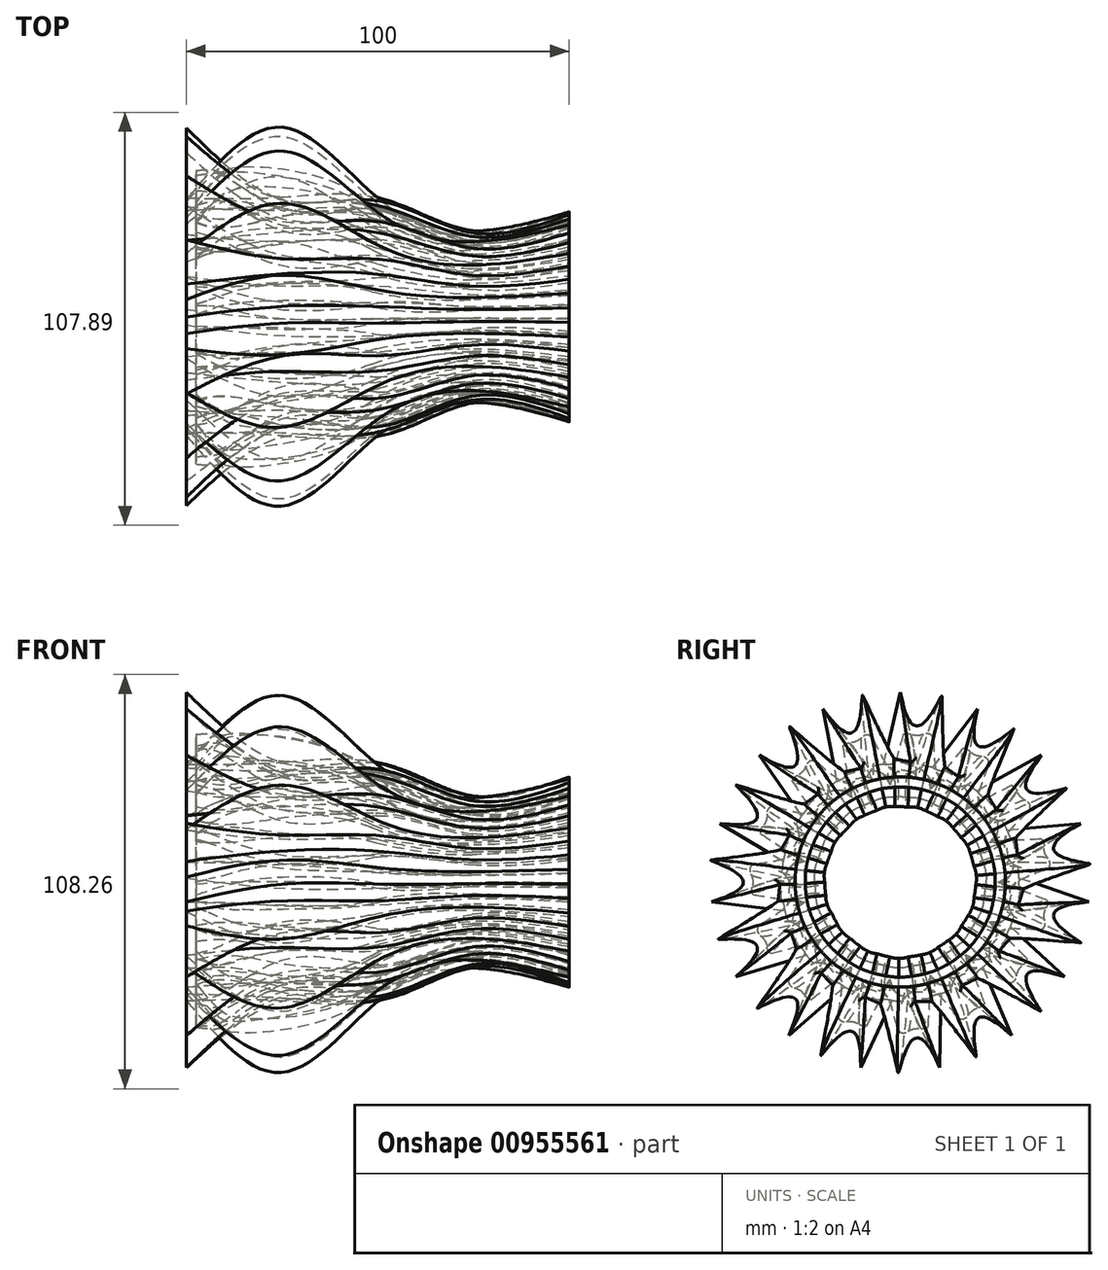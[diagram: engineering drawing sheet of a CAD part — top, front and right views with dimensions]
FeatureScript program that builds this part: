
annotation { "Feature Type Name" : "Feature", "Feature Type Description" : "" }
export const myFeature = defineFeature(function(context is Context, id is Id, definition is map)
    precondition{}
    {
        {
            var Q0;
            Q0=qCreatedBy(makeId("Right.planeOp"),FACE);
            var sketch = newSketch(context, id + "F0", { "sketchPlane" : qUnion([Q0])});
            skCircle(sketch, "E0", {"center": v(0, 0) * mm, "radius": 31.06 * mm});
            skLineSegment(sketch, "E1", {"start": v(-4.34, 30.75) * mm, "end": v(0, 49.56) * mm});
            skLineSegment(sketch, "E2", {"start": v(0, 49.56) * mm, "end": v(4.53, 30.72) * mm});
            skLineSegment(sketch, "E3.1.0", {"start": v(-20.16, 45.27) * mm, "end": v(-8.36, 29.91) * mm});
            skLineSegment(sketch, "E3.1.1", {"start": v(-16.47, 26.33) * mm, "end": v(-20.16, 45.27) * mm});
            skLineSegment(sketch, "E3.2.0", {"start": v(-36.83, 33.16) * mm, "end": v(-19.8, 23.92) * mm});
            skLineSegment(sketch, "E3.2.1", {"start": v(-25.76, 17.35) * mm, "end": v(-36.83, 33.16) * mm});
            skLineSegment(sketch, "E3.3.0", {"start": v(-47.13, 15.31) * mm, "end": v(-27.82, 13.8) * mm});
            skLineSegment(sketch, "E3.3.1", {"start": v(-30.59, 5.38) * mm, "end": v(-47.13, 15.31) * mm});
            skLineSegment(sketch, "E3.4.0", {"start": v(-49.29, -5.18) * mm, "end": v(-31.03, 1.3) * mm});
            skLineSegment(sketch, "E3.4.1", {"start": v(-30.13, -7.53) * mm, "end": v(-49.29, -5.18) * mm});
            skLineSegment(sketch, "E3.5.0", {"start": v(-42.92, -24.78) * mm, "end": v(-28.87, -11.44) * mm});
            skLineSegment(sketch, "E3.5.1", {"start": v(-24.46, -19.13) * mm, "end": v(-42.92, -24.78) * mm});
            skLineSegment(sketch, "E3.6.0", {"start": v(-29.13, -40.1) * mm, "end": v(-21.72, -22.2) * mm});
            skLineSegment(sketch, "E3.6.1", {"start": v(-14.56, -27.43) * mm, "end": v(-29.13, -40.1) * mm});
            skLineSegment(sketch, "E3.7.0", {"start": v(-10.3, -48.48) * mm, "end": v(-10.82, -29.11) * mm});
            skLineSegment(sketch, "E3.7.1", {"start": v(-2.15, -30.98) * mm, "end": v(-10.3, -48.48) * mm});
            skLineSegment(sketch, "E3.8.0", {"start": v(10.3, -48.48) * mm, "end": v(1.96, -31) * mm});
            skLineSegment(sketch, "E3.8.1", {"start": v(10.64, -29.18) * mm, "end": v(10.3, -48.48) * mm});
            skLineSegment(sketch, "E3.9.0", {"start": v(29.13, -40.1) * mm, "end": v(14.4, -27.52) * mm});
            skLineSegment(sketch, "E3.9.1", {"start": v(21.59, -22.33) * mm, "end": v(29.13, -40.1) * mm});
            skLineSegment(sketch, "E3.10.0", {"start": v(42.92, -24.78) * mm, "end": v(24.34, -19.29) * mm});
            skLineSegment(sketch, "E3.10.1", {"start": v(28.8, -11.62) * mm, "end": v(42.92, -24.78) * mm});
            skLineSegment(sketch, "E3.11.0", {"start": v(49.29, -5.18) * mm, "end": v(30.08, -7.72) * mm});
            skLineSegment(sketch, "E3.11.1", {"start": v(31.04, 1.1) * mm, "end": v(49.29, -5.18) * mm});
            skLineSegment(sketch, "E3.12.0", {"start": v(47.13, 15.31) * mm, "end": v(30.62, 5.19) * mm});
            skLineSegment(sketch, "E3.12.1", {"start": v(27.9, 13.63) * mm, "end": v(47.13, 15.31) * mm});
            skLineSegment(sketch, "E3.13.0", {"start": v(36.83, 33.16) * mm, "end": v(25.86, 17.2) * mm});
            skLineSegment(sketch, "E3.13.1", {"start": v(19.95, 23.8) * mm, "end": v(36.83, 33.16) * mm});
            skLineSegment(sketch, "E3.14.0", {"start": v(20.16, 45.27) * mm, "end": v(16.64, 26.22) * mm});
            skLineSegment(sketch, "E3.14.1", {"start": v(8.54, 29.86) * mm, "end": v(20.16, 45.27) * mm});
            skSolve(sketch);
        }
        {
            var Q0;
            Q0=qCreatedBy(makeId("Right.planeOp"),FACE);
            cPlane(context, id + "F1", {"entities" : qUnion([Q0]), "cplaneType" : CPlaneType.OFFSET, "offset" : 25 * mm, "width" : 150 * mm, "height" : 150 * mm});
        }
        {
            var Q0;
            Q0=qCreatedBy(id+"F1.planeOp",FACE);
            var sketch = newSketch(context, id + "F2", { "sketchPlane" : qUnion([Q0])});
            skCircle(sketch, "E4", {"center": v(0, 0) * mm, "radius": 31.34 * mm});
            skLineSegment(sketch, "E5", {"start": v(2.73, 31.22) * mm, "end": v(10.87, 48.55) * mm});
            skLineSegment(sketch, "E6", {"start": v(10.87, 48.55) * mm, "end": v(11.2, 29.27) * mm});
            skLineSegment(sketch, "E7.1.0", {"start": v(-9.82, 48.77) * mm, "end": v(-1.67, 31.3) * mm});
            skLineSegment(sketch, "E7.1.1", {"start": v(-10.2, 29.63) * mm, "end": v(-9.82, 48.77) * mm});
            skLineSegment(sketch, "E7.2.0", {"start": v(-28.8, 40.56) * mm, "end": v(-14.25, 27.92) * mm});
            skLineSegment(sketch, "E7.2.1", {"start": v(-21.38, 22.92) * mm, "end": v(-28.8, 40.56) * mm});
            skLineSegment(sketch, "E7.3.0", {"start": v(-42.81, 25.34) * mm, "end": v(-24.37, 19.7) * mm});
            skLineSegment(sketch, "E7.3.1", {"start": v(-28.85, 12.24) * mm, "end": v(-42.81, 25.34) * mm});
            skLineSegment(sketch, "E7.4.0", {"start": v(-49.42, 5.74) * mm, "end": v(-30.28, 8.09) * mm});
            skLineSegment(sketch, "E7.4.1", {"start": v(-31.34, -0.55) * mm, "end": v(-49.42, 5.74) * mm});
            skLineSegment(sketch, "E7.5.0", {"start": v(-47.48, -14.86) * mm, "end": v(-30.95, -4.93) * mm});
            skLineSegment(sketch, "E7.5.1", {"start": v(-28.4, -13.25) * mm, "end": v(-47.48, -14.86) * mm});
            skLineSegment(sketch, "E7.6.0", {"start": v(-37.33, -32.89) * mm, "end": v(-26.27, -17.1) * mm});
            skLineSegment(sketch, "E7.6.1", {"start": v(-20.56, -23.66) * mm, "end": v(-37.33, -32.89) * mm});
            skLineSegment(sketch, "E7.7.0", {"start": v(-20.73, -45.23) * mm, "end": v(-17.05, -26.3) * mm});
            skLineSegment(sketch, "E7.7.1", {"start": v(-9.16, -29.98) * mm, "end": v(-20.73, -45.23) * mm});
            skLineSegment(sketch, "E7.8.0", {"start": v(-0.54, -49.75) * mm, "end": v(-4.88, -30.96) * mm});
            skLineSegment(sketch, "E7.8.1", {"start": v(3.82, -31.1) * mm, "end": v(-0.54, -49.75) * mm});
            skLineSegment(sketch, "E7.9.0", {"start": v(19.74, -45.67) * mm, "end": v(8.14, -30.27) * mm});
            skLineSegment(sketch, "E7.9.1", {"start": v(16.15, -26.86) * mm, "end": v(19.74, -45.67) * mm});
            skLineSegment(sketch, "E7.10.0", {"start": v(36.61, -33.69) * mm, "end": v(19.74, -24.34) * mm});
            skLineSegment(sketch, "E7.10.1", {"start": v(25.68, -17.97) * mm, "end": v(36.61, -33.69) * mm});
            skLineSegment(sketch, "E7.11.0", {"start": v(47.15, -15.89) * mm, "end": v(27.94, -14.2) * mm});
            skLineSegment(sketch, "E7.11.1", {"start": v(30.77, -5.98) * mm, "end": v(47.15, -15.89) * mm});
            skLineSegment(sketch, "E7.12.0", {"start": v(49.53, 4.66) * mm, "end": v(31.3, -1.62) * mm});
            skLineSegment(sketch, "E7.12.1", {"start": v(30.54, 7.06) * mm, "end": v(49.53, 4.66) * mm});
            skLineSegment(sketch, "E7.13.0", {"start": v(43.35, 24.4) * mm, "end": v(29.25, 11.26) * mm});
            skLineSegment(sketch, "E7.13.1", {"start": v(25.03, 18.87) * mm, "end": v(43.35, 24.4) * mm});
            skLineSegment(sketch, "E7.14.0", {"start": v(29.68, 39.93) * mm, "end": v(22.15, 22.18) * mm});
            skLineSegment(sketch, "E7.14.1", {"start": v(15.2, 27.42) * mm, "end": v(29.68, 39.93) * mm});
            skSolve(sketch);
        }
        {
            var Q0;
            Q0=qCreatedBy(id+"F1.planeOp",FACE);
            cPlane(context, id + "F3", {"entities" : qUnion([Q0]), "cplaneType" : CPlaneType.OFFSET, "offset" : 25 * mm, "width" : 150 * mm, "height" : 150 * mm});
        }
        {
            var Q0;
            Q0=qCreatedBy(id+"F3.planeOp",FACE);
            var sketch = newSketch(context, id + "F4", { "sketchPlane" : qUnion([Q0])});
            skCircle(sketch, "E8", {"center": v(0, 0) * mm, "radius": 31.19 * mm});
            skSolve(sketch);
        }
        {
            var Q0;
            Q0=qCreatedBy(id+"F3.planeOp",FACE);
            cPlane(context, id + "F5", {"entities" : qUnion([Q0]), "cplaneType" : CPlaneType.OFFSET, "offset" : 25 * mm, "width" : 150 * mm, "height" : 150 * mm});
        }
        {
            var Q0;
            Q0=qCreatedBy(id+"F5.planeOp",FACE);
            var sketch = newSketch(context, id + "F6", { "sketchPlane" : qUnion([Q0])});
            skCircle(sketch, "E9", {"center": v(0, 0) * mm, "radius": 22.46 * mm});
            skSolve(sketch);
        }
        {
            var Q0;
            Q0=qCreatedBy(id+"F5.planeOp",FACE);
            cPlane(context, id + "F7", {"entities" : qUnion([Q0]), "cplaneType" : CPlaneType.OFFSET, "offset" : 25 * mm, "width" : 150 * mm, "height" : 150 * mm});
        }
        {
            var Q0;
            Q0=qCreatedBy(id+"F7.planeOp",FACE);
            var sketch = newSketch(context, id + "F8", { "sketchPlane" : qUnion([Q0])});
            skCircle(sketch, "E10", {"center": v(0, 0) * mm, "radius": 27.46 * mm});
            skSolve(sketch);
        }
        {
            var Q0;
            Q0 = qSketchRegion(id + "F0", true);
            var Q1;
            Q1 = qSketchRegion(id + "F2", true);
            var Q2;
            Q2 = qSketchRegion(id + "F4", true);
            var Q3;
            Q3 = qSketchRegion(id + "F6", true);
            var Q4;
            Q4 = qSketchRegion(id + "F8", true);
            loft(context, id + "F9", {"sheetProfilesArray" : [{ "sheetProfileEntities" : qUnion([Q0]) }, { "sheetProfileEntities" : qUnion([Q1]) }, { "sheetProfileEntities" : qUnion([Q2]) }, { "sheetProfileEntities" : qUnion([Q3]) }, { "sheetProfileEntities" : qUnion([Q4]) }]});
        }
        {
            var Q0;
            Q0=makeQuery(id+"F9.opLoft","CAP_FACE",FACE,{"disambiguationData":[OSD([makeQuery(id+"F8.imprint","IMPRINT",FACE,{"disambiguationData":[TD([[makeQuery(id+"F8.imprint","IMPRINT",EDGE,{"derivedFrom":sQuery(id+"F8.wireOp",EDGE,"E10")}),1.0]])]})])],"isStart":true});
            shell(context, id + "F10", {"entities" : qUnion([Q0]), "thickness" : 2.5 * mm});
        }
    });
